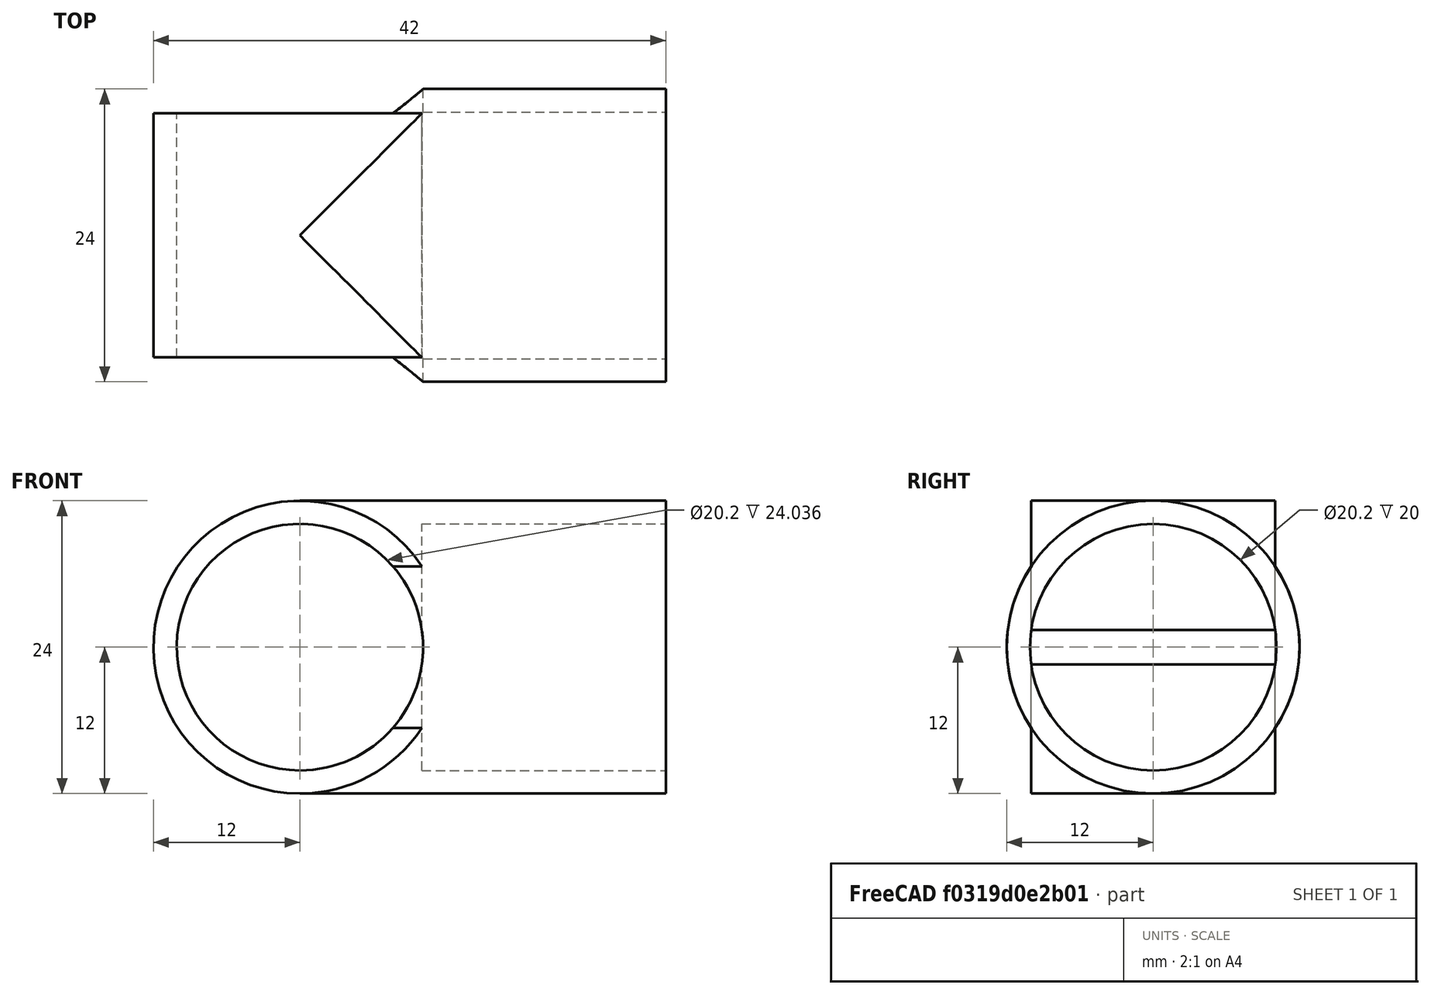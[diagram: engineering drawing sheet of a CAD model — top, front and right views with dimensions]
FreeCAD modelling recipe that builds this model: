
FCSTD DOCUMENT  (FreeCAD 0.17R13522 (Git))
Label: connector-stand
License: All rights reserved
LicenseURL: http://en.wikipedia.org/wiki/All_rights_reserved
objects: Part::Cylinder×4, Part::MultiFuse×2, Part::Cut×1
note: 7 computed .brp shape members not serialized (recipe doc carries the construction recipe); baked Part::Feature solids carry a one-line shape summary decoded from their .brp

FEATURE [Part::Cylinder] Cylinder
  Angle = 360
  AttacherType = Attacher::AttachEngine3D
  Height = 30
  Placement = pos=(0,0,0) rot=(0,1,0;1.5708rad)
  Radius = 12
FEATURE [Part::Cylinder] Cylinder001
  Angle = 360
  AttacherType = Attacher::AttachEngine3D
  Height = 20
  Placement = pos=(0,-10,0) rot=(0.57735,-0.57735,-0.57735;4.18879rad)
  Radius = 12
FEATURE [Part::Cylinder] Cylinder002
  Angle = 360
  AttacherType = Attacher::AttachEngine3D
  Height = 20
  Placement = pos=(10,0,0) rot=(0,1,0;1.5708rad)
  Radius = 10.1
FEATURE [Part::Cylinder] Cylinder003
  Angle = 360
  AttacherType = Attacher::AttachEngine3D
  Height = 30
  Placement = pos=(0,-15,0) rot=(0.57735,-0.57735,-0.57735;4.18879rad)
  Radius = 10.1
FEATURE [Part::MultiFuse] Fusion  label="Positive Fusion"
  Shapes = -> [Cylinder001,Cylinder]
FEATURE [Part::MultiFuse] Fusion001  label="Negative Fusion"
  Shapes = -> [Cylinder003,Cylinder002]
FEATURE [Part::Cut] Cut
  Base = -> Fusion
  Tool = -> Fusion001
